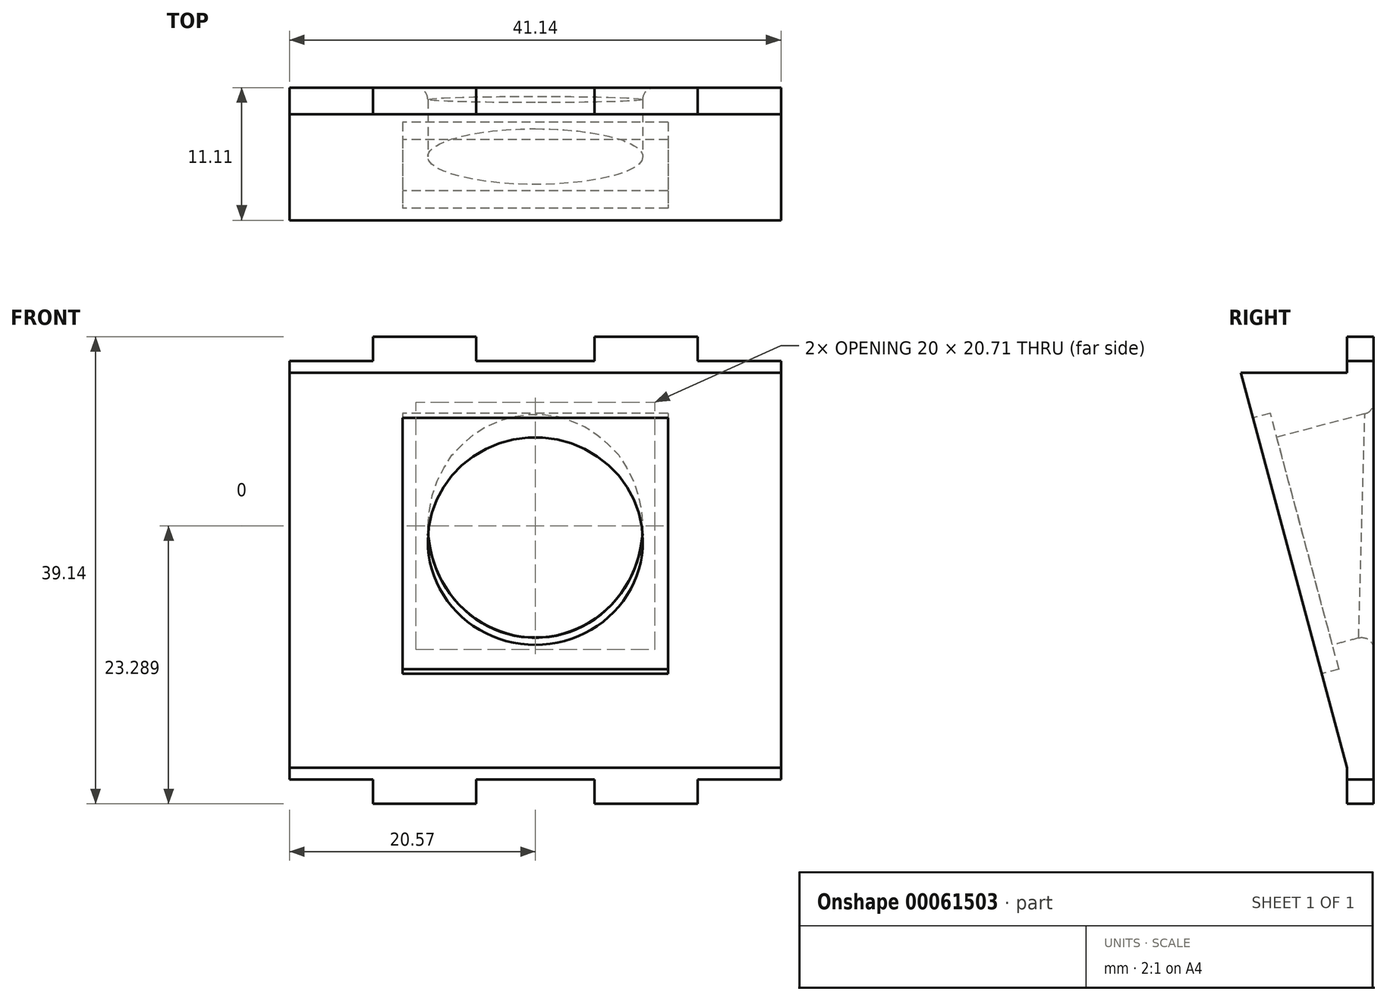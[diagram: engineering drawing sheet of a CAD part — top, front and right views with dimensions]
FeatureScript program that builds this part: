
annotation { "Feature Type Name" : "Feature", "Feature Type Description" : "" }
export const myFeature = defineFeature(function(context is Context, id is Id, definition is map)
    precondition{}
    {
        {
            var Q0;
            Q0=qCreatedBy(makeId("Front.planeOp"),FACE);
            var sketch = newSketch(context, id + "F0", { "sketchPlane" : qUnion([Q0])});
            skLineSegment(sketch, "E0.rect.bottom", {"start": v(13.59, 19.57) * mm, "end": v(4.95, 19.57) * mm});
            skLineSegment(sketch, "E0.rect.top", {"start": v(13.59, -19.57) * mm, "end": v(4.95, -19.57) * mm});
            skLineSegment(sketch, "E0.rect.left", {"start": v(20.57, 17.54) * mm, "end": v(20.57, -17.54) * mm});
            skLineSegment(sketch, "E0.rect.right", {"start": v(-20.57, 17.54) * mm, "end": v(-20.57, -17.54) * mm});
            skPoint(sketch, "E0.rect.middle", {"position": v(0, 0) * mm});
            skLineSegment(sketch, "E1", {"start": v(-20.57, 17.54) * mm, "end": v(-13.59, 17.54) * mm});
            skLineSegment(sketch, "E2", {"start": v(-13.59, 19.57) * mm, "end": v(-13.59, 17.54) * mm});
            skPoint(sketch, "E3.orphan", {"position": v(-20.57, 19.57) * mm});
            skLineSegment(sketch, "E4", {"start": v(-4.95, 19.57) * mm, "end": v(-4.95, 17.54) * mm});
            skLineSegment(sketch, "E5.trimOffspring", {"start": v(-4.95, 17.54) * mm, "end": v(4.95, 17.54) * mm});
            skLineSegment(sketch, "E6", {"start": v(4.95, 19.57) * mm, "end": v(4.95, 17.54) * mm});
            skLineSegment(sketch, "E7", {"start": v(13.59, 19.57) * mm, "end": v(13.59, 17.54) * mm});
            skLineSegment(sketch, "E8.trimOffspring", {"start": v(-4.95, 19.57) * mm, "end": v(-13.59, 19.57) * mm});
            skLineSegment(sketch, "E9.trimOffspring", {"start": v(13.59, 17.54) * mm, "end": v(20.57, 17.54) * mm});
            skPoint(sketch, "E10.orphan", {"position": v(20.57, 19.57) * mm});
            skLineSegment(sketch, "E11", {"start": v(-20.57, -17.54) * mm, "end": v(-13.59, -17.54) * mm});
            skLineSegment(sketch, "E12", {"start": v(-13.59, -17.54) * mm, "end": v(-13.59, -19.57) * mm});
            skLineSegment(sketch, "E13", {"start": v(-4.95, -17.54) * mm, "end": v(-4.95, -19.57) * mm});
            skLineSegment(sketch, "E14", {"start": v(4.95, -17.54) * mm, "end": v(4.95, -19.57) * mm});
            skLineSegment(sketch, "E15", {"start": v(13.59, -17.54) * mm, "end": v(13.59, -19.57) * mm});
            skPoint(sketch, "E16.orphan", {"position": v(20.57, -19.57) * mm});
            skLineSegment(sketch, "E17.trimOffspring", {"start": v(13.59, -17.54) * mm, "end": v(20.57, -17.54) * mm});
            skLineSegment(sketch, "E18.trimOffspring", {"start": v(-4.95, -19.57) * mm, "end": v(-13.59, -19.57) * mm});
            skLineSegment(sketch, "E19.trimOffspring", {"start": v(-4.95, -17.54) * mm, "end": v(4.95, -17.54) * mm});
            skPoint(sketch, "E20.orphan", {"position": v(-20.57, -19.57) * mm});
            skPoint(sketch, "E21.visualSharp", {"position": v(13.97, 15.2) * mm});
            skPoint(sketch, "E22.visualSharp", {"position": v(-13.97, -15.2) * mm});
            skPoint(sketch, "E23.visualSharp", {"position": v(-18.36, -15.2) * mm});
            skPoint(sketch, "E24.visualSharp", {"position": v(-16.18, -15.2) * mm});
            skLineSegment(sketch, "E25", {"start": v(-20.57, -17.54) * mm, "end": v(-20.57, -16.54) * mm});
            skLineSegment(sketch, "E26", {"start": v(-20.57, -16.54) * mm, "end": v(20.57, -16.54) * mm});
            skLineSegment(sketch, "E27", {"start": v(-20.57, 0) * mm, "end": v(20.57, 0) * mm, "construction": true});
            skLineSegment(sketch, "E28.MirrorCS", {"start": v(-20.57, 16.54) * mm, "end": v(20.57, 16.54) * mm});
            skSolve(sketch);
        }
        {
            var Q0;
            Q0=makeQuery(id+"F0.imprint","IMPRINT",FACE,{"disambiguationData":[TD([[makeQuery(id+"F0.imprint","IMPRINT",EDGE,{"derivedFrom":sQuery(id+"F0.wireOp",EDGE,"E0.rect.bottom")}),1.0]])]});
            var Q1;
            Q1=makeQuery(id+"F0.imprint","IMPRINT",FACE,{"disambiguationData":[TD([[makeQuery(id+"F0.imprint","IMPRINT",EDGE,{"derivedFrom":sQuery(id+"F0.wireOp",EDGE,"E0.rect.top")}),-1.0]])]});
            extrude(context, id + "F1", {"entities" : qUnion([Q0, Q1]), "depth" : 2.25 * mm});
        }
        {
            var Q0;
            {var subQ0=sQuery(id+"F0.wireOp",EDGE,"E26");Q0=makeQuery(id+"F0.imprint","IMPRINT",FACE,{"disambiguationData":[TD([[makeQuery(id+"F0.imprint","IMPRINT",EDGE,{"derivedFrom":subQ0}),1.0]])]});}
            extrude(context, id + "F2", {"entities" : qUnion([Q0]), "depth" : 15 * mm});
        }
        {
            var Q0;
            Q0=makeQuery(id+"F1.opExtrude","SWEPT_BODY",BODY,{"disambiguationData":[OSD([sQuery(id+"F0.wireOp",EDGE,"E0.rect.bottom"),sQuery(id+"F0.wireOp",EDGE,"E0.rect.left"),sQuery(id+"F0.wireOp",EDGE,"E0.rect.right"),sQuery(id+"F0.wireOp",EDGE,"E1"),sQuery(id+"F0.wireOp",EDGE,"E2"),sQuery(id+"F0.wireOp",EDGE,"E4"),sQuery(id+"F0.wireOp",EDGE,"E5.trimOffspring"),sQuery(id+"F0.wireOp",EDGE,"E6"),sQuery(id+"F0.wireOp",EDGE,"E7"),sQuery(id+"F0.wireOp",EDGE,"E8.trimOffspring"),sQuery(id+"F0.wireOp",EDGE,"E9.trimOffspring"),sQuery(id+"F0.wireOp",EDGE,"E28.MirrorCS")])]});
            var Q1;
            Q1=makeQuery(id+"F1.opExtrude","SWEPT_BODY",BODY,{"disambiguationData":[OSD([sQuery(id+"F0.wireOp",EDGE,"E0.rect.top"),sQuery(id+"F0.wireOp",EDGE,"E0.rect.left"),sQuery(id+"F0.wireOp",EDGE,"E11"),sQuery(id+"F0.wireOp",EDGE,"E12"),sQuery(id+"F0.wireOp",EDGE,"E13"),sQuery(id+"F0.wireOp",EDGE,"E14"),sQuery(id+"F0.wireOp",EDGE,"E15"),sQuery(id+"F0.wireOp",EDGE,"E17.trimOffspring"),sQuery(id+"F0.wireOp",EDGE,"E18.trimOffspring"),sQuery(id+"F0.wireOp",EDGE,"E19.trimOffspring"),sQuery(id+"F0.wireOp",EDGE,"E25"),sQuery(id+"F0.wireOp",EDGE,"E26")])]});
            var Q2;
            Q2=makeQuery(id+"F2.opExtrude","SWEPT_BODY",BODY,{"disambiguationData":[OSD([sQuery(id+"F0.wireOp",EDGE,"E0.rect.left"),sQuery(id+"F0.wireOp",EDGE,"E0.rect.right"),sQuery(id+"F0.wireOp",EDGE,"4804f3b9-56da-4af5-8868-d183c89fbcf5.bottom"),sQuery(id+"F0.wireOp",EDGE,"4804f3b9-56da-4af5-8868-d183c89fbcf5.top"),sQuery(id+"F0.wireOp",EDGE,"4804f3b9-56da-4af5-8868-d183c89fbcf5.left"),sQuery(id+"F0.wireOp",EDGE,"4804f3b9-56da-4af5-8868-d183c89fbcf5.right"),sQuery(id+"F0.wireOp",EDGE,"97199a84-c1ce-4e26-b22d-6798a98a9595.bottom"),sQuery(id+"F0.wireOp",EDGE,"97199a84-c1ce-4e26-b22d-6798a98a9595.top"),sQuery(id+"F0.wireOp",EDGE,"97199a84-c1ce-4e26-b22d-6798a98a9595.left"),sQuery(id+"F0.wireOp",EDGE,"97199a84-c1ce-4e26-b22d-6798a98a9595.right"),sQuery(id+"F0.wireOp",EDGE,"5fc2c682-06e9-4b61-9a66-a73d499bdc7a.filletArc"),sQuery(id+"F0.wireOp",EDGE,"1b878f1c-4d8f-48ab-8b4b-3197ee4bca85.filletArc"),sQuery(id+"F0.wireOp",EDGE,"2340a9f0-8645-437b-8370-240680a500a8.filletArc"),sQuery(id+"F0.wireOp",EDGE,"5a49e16a-16d5-437c-897c-d39f08ae84b2.filletArc"),sQuery(id+"F0.wireOp",EDGE,"544242f5-4153-422d-88da-9b6d3b59cea0.filletArc"),sQuery(id+"F0.wireOp",EDGE,"0b8d7d45-7896-46b3-a7aa-3d18b2ac9636.filletArc"),sQuery(id+"F0.wireOp",EDGE,"E23.filletArc"),sQuery(id+"F0.wireOp",EDGE,"E24.filletArc"),sQuery(id+"F0.wireOp",EDGE,"afc62a43-f465-44a6-a353-0f6553cd04b5.bottom"),sQuery(id+"F0.wireOp",EDGE,"afc62a43-f465-44a6-a353-0f6553cd04b5.top"),sQuery(id+"F0.wireOp",EDGE,"afc62a43-f465-44a6-a353-0f6553cd04b5.left"),sQuery(id+"F0.wireOp",EDGE,"afc62a43-f465-44a6-a353-0f6553cd04b5.right"),sQuery(id+"F0.wireOp",EDGE,"E26"),sQuery(id+"F0.wireOp",EDGE,"E28.MirrorCS")])]});
            booleanBodies(context, id + "F3", {"operationType" : BooleanOperationType.UNION, "tools" : qUnion([Q0, Q1, Q2])});
        }
        {
            var Q0;
            {var subQ0=sQuery(id+"F0.wireOp",EDGE,"E0.rect.left");Q0=makeQuery(id+"F3.opBoolean","MERGE",FACE,{"derivedFrom":[makeQuery(id+"F1.opExtrude","SWEPT_FACE",FACE,{"disambiguationData":[OSD([subQ0]),TDD([makeQuery(id+"F0.imprint","IMPRINT",EDGE,{"disambiguationData":[TD([[makeQuery(id+"F0.imprint","INTERSECT",VERTEX,{"derivedFrom":[subQ0,sQuery(id+"F0.wireOp",EDGE,"E9.trimOffspring")]}),-1.0]])],"derivedFrom":subQ0})])]}),makeQuery(id+"F1.opExtrude","SWEPT_FACE",FACE,{"disambiguationData":[OSD([subQ0]),TDD([makeQuery(id+"F0.imprint","IMPRINT",EDGE,{"disambiguationData":[TD([[makeQuery(id+"F0.imprint","INTERSECT",VERTEX,{"derivedFrom":[subQ0,sQuery(id+"F0.wireOp",EDGE,"E17.trimOffspring")]}),1.0]])],"derivedFrom":subQ0})])]}),makeQuery(id+"F2.opExtrude","SWEPT_FACE",FACE,{"disambiguationData":[OSD([subQ0])]})]});}
            var sketch = newSketch(context, id + "F4", { "sketchPlane" : qUnion([Q0])});
            skLineSegment(sketch, "E29", {"start": v(-2.25, -16.54) * mm, "end": v(-15, -16.54) * mm});
            skLineSegment(sketch, "E30", {"start": v(-15, -16.54) * mm, "end": v(-15, 16.54) * mm});
            skLineSegment(sketch, "E31", {"start": v(-2.25, -16.54) * mm, "end": v(-11.11, 16.54) * mm});
            skLineSegment(sketch, "E32", {"start": v(-15, 16.54) * mm, "end": v(-11.11, 16.54) * mm});
            skSolve(sketch);
        }
        {
            var Q0;
            Q0=makeQuery(id+"F4.imprint","IMPRINT",FACE,{"disambiguationData":[TD([[makeQuery(id+"F4.imprint","IMPRINT",EDGE,{"derivedFrom":sQuery(id+"F4.wireOp",EDGE,"E29")}),1.0]])]});
            extrude(context, id + "F5", {"entities" : qUnion([Q0]), "operationType" : NewBodyOperationType.REMOVE, "oppositeDirection" : true, "depth" : 50 * mm});
        }
        {
            var Q0;
            Q0=makeQuery(id+"F5.boolean.opBoolean","COPY",FACE,{"derivedFrom":makeQuery(id+"F5.opExtrude","SWEPT_FACE",FACE,{"disambiguationData":[OSD([sQuery(id+"F4.wireOp",EDGE,"E31")])]})});
            var sketch = newSketch(context, id + "F6", { "sketchPlane" : qUnion([Q0])});
            skLineSegment(sketch, "E33", {"start": v(0, 18.85) * mm, "end": v(0, 3.85) * mm});
            skCircle(sketch, "E34", {"center": v(0, 3.85) * mm, "radius": 9 * mm});
            skLineSegment(sketch, "E35.rect.bottom", {"start": v(11.1, -7.25) * mm, "end": v(-11.1, -7.25) * mm});
            skLineSegment(sketch, "E35.rect.top", {"start": v(11.1, 14.95) * mm, "end": v(-11.1, 14.95) * mm});
            skLineSegment(sketch, "E35.rect.left", {"start": v(11.1, -7.25) * mm, "end": v(11.1, 14.95) * mm});
            skLineSegment(sketch, "E35.rect.right", {"start": v(-11.1, -7.25) * mm, "end": v(-11.1, 14.95) * mm});
            skSolve(sketch);
        }
        {
            var Q0;
            Q0=makeQuery(id+"F6.imprint","IMPRINT",FACE,{"disambiguationData":[TD([[makeQuery(id+"F6.imprint","IMPRINT",EDGE,{"derivedFrom":sQuery(id+"F6.wireOp",EDGE,"E34")}),1.0]])]});
            extrude(context, id + "F7", {"entities" : qUnion([Q0]), "operationType" : NewBodyOperationType.REMOVE, "endBound" : BoundingType.THROUGH_ALL, "oppositeDirection" : true, "depth" : 25 * mm});
        }
        {
            var Q0;
            Q0=makeQuery(id+"F6.imprint","IMPRINT",FACE,{"disambiguationData":[TD([[makeQuery(id+"F6.imprint","IMPRINT",EDGE,{"derivedFrom":sQuery(id+"F6.wireOp",EDGE,"E34")}),-1.0]])]});
            extrude(context, id + "F8", {"entities" : qUnion([Q0]), "operationType" : NewBodyOperationType.REMOVE, "oppositeDirection" : true, "depth" : 1.5 * mm});
        }
        {
            var Q0;
            {var subQ0=sQuery(id+"F0.wireOp",EDGE,"E28.MirrorCS");var subQ1=sQuery(id+"F0.wireOp",EDGE,"E26");var subQ2=sQuery(id+"F0.wireOp",EDGE,"E0.rect.right");var subQ3=sQuery(id+"F0.wireOp",EDGE,"E0.rect.left");Q0=makeQuery(id+"F7.boolean.opBoolean","INTERSECT",EDGE,{"derivedFrom":[makeQuery(id+"F3.opBoolean","MERGE",FACE,{"derivedFrom":[makeQuery(id+"F1.opExtrude","CAP_FACE",FACE,{"disambiguationData":[OSD([sQuery(id+"F0.wireOp",EDGE,"E0.rect.bottom"),subQ3,subQ2,sQuery(id+"F0.wireOp",EDGE,"E1"),sQuery(id+"F0.wireOp",EDGE,"E2"),sQuery(id+"F0.wireOp",EDGE,"E4"),sQuery(id+"F0.wireOp",EDGE,"E5.trimOffspring"),sQuery(id+"F0.wireOp",EDGE,"E6"),sQuery(id+"F0.wireOp",EDGE,"E7"),sQuery(id+"F0.wireOp",EDGE,"E8.trimOffspring"),sQuery(id+"F0.wireOp",EDGE,"E9.trimOffspring"),subQ0])],"isStart":true}),makeQuery(id+"F1.opExtrude","CAP_FACE",FACE,{"disambiguationData":[OSD([sQuery(id+"F0.wireOp",EDGE,"E0.rect.top"),subQ3,sQuery(id+"F0.wireOp",EDGE,"E11"),sQuery(id+"F0.wireOp",EDGE,"E12"),sQuery(id+"F0.wireOp",EDGE,"E13"),sQuery(id+"F0.wireOp",EDGE,"E14"),sQuery(id+"F0.wireOp",EDGE,"E15"),sQuery(id+"F0.wireOp",EDGE,"E17.trimOffspring"),sQuery(id+"F0.wireOp",EDGE,"E18.trimOffspring"),sQuery(id+"F0.wireOp",EDGE,"E19.trimOffspring"),sQuery(id+"F0.wireOp",EDGE,"E25"),subQ1])],"isStart":true}),makeQuery(id+"F2.opExtrude","CAP_FACE",FACE,{"disambiguationData":[OSD([subQ3,subQ2,subQ1,subQ0])],"isStart":true})]}),makeQuery(id+"F7.opExtrude","SWEPT_FACE",FACE,{"disambiguationData":[OSD([sQuery(id+"F6.wireOp",EDGE,"E34")])]})]});}
            var Q1;
            Q1=makeQuery(id+"F8.boolean.opBoolean","COPY",EDGE,{"derivedFrom":makeQuery(id+"F8.opExtrude","CAP_EDGE",EDGE,{"disambiguationData":[OSD([sQuery(id+"F6.wireOp",EDGE,"E34")])],"isStart":false})});
            fillet(context, id + "F9", {"entities" : qUnion([Q0, Q1]), "radius" : 1 * mm, "tangentPropagation" : true, "allowEdgeOverflow" : false});
        }
    });
